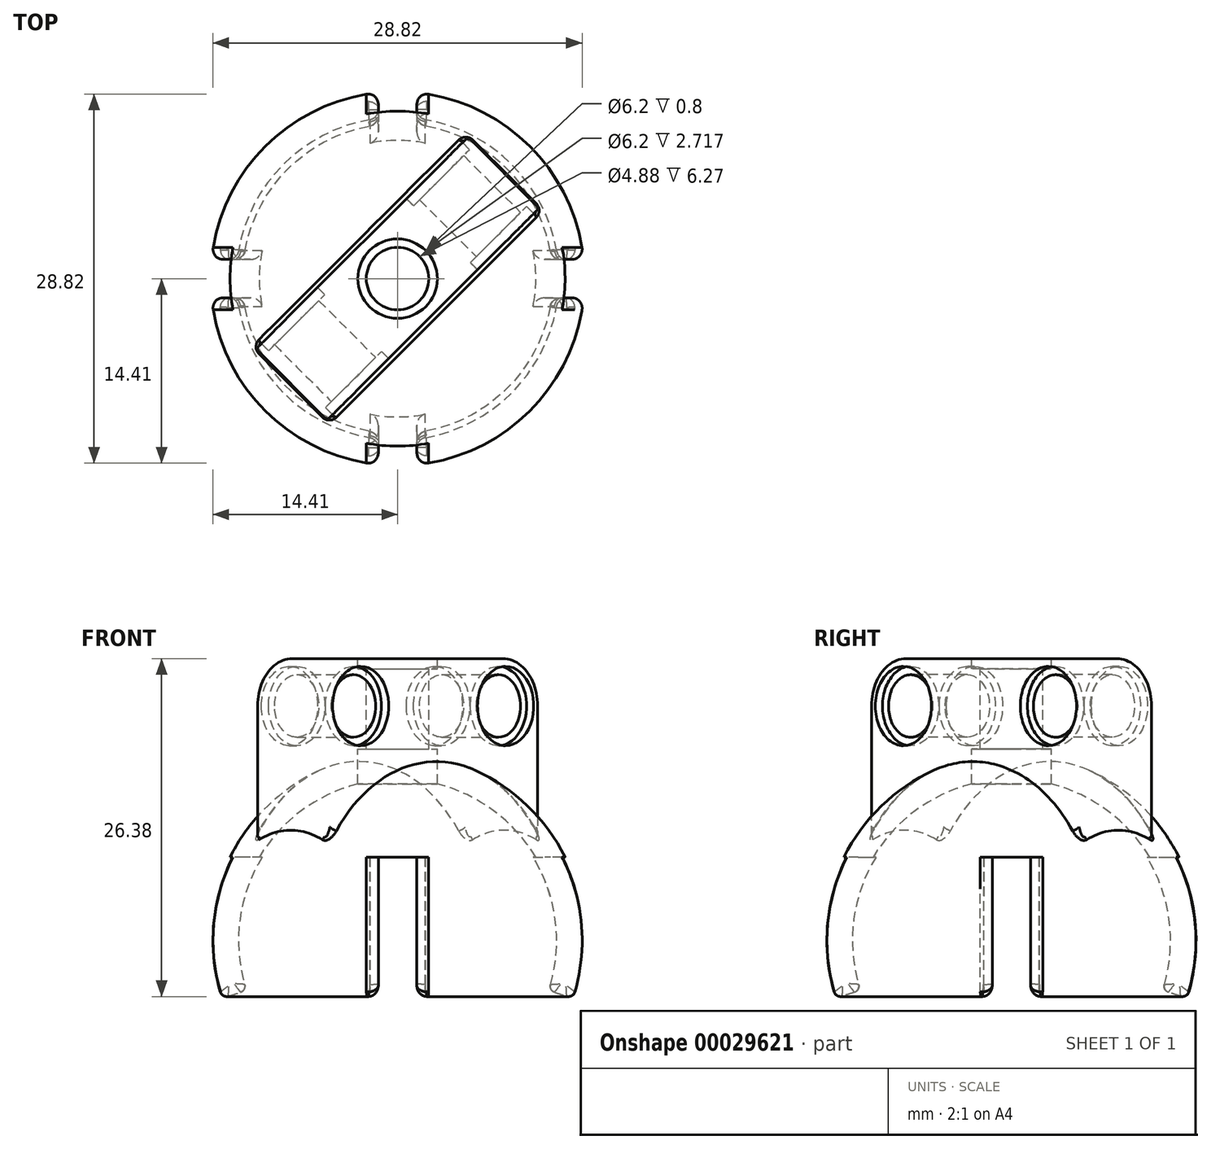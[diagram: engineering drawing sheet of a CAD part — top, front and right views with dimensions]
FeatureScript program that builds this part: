
annotation { "Feature Type Name" : "Feature", "Feature Type Description" : "" }
export const myFeature = defineFeature(function(context is Context, id is Id, definition is map)
    precondition{}
    {
        {
            var Q0;
            Q0=qCreatedBy(makeId("Front.planeOp"),FACE);
            var sketch = newSketch(context, id + "F0", { "sketchPlane" : qUnion([Q0])});
            skArc(sketch, "E0", {"start": v(12.12, -3.43) * mm, "mid": v(10.05, 7.6) * mm, "end": v(0, 12.6) * mm});
            skArc(sketch, "E1", {"start": v(14.04, -4.02) * mm, "mid": v(11.66, 8.79) * mm, "end": v(0, 14.6) * mm});
            skLineSegment(sketch, "E2", {"start": v(12.45, -4.05) * mm, "end": v(13.4, -4.35) * mm});
            skLineSegment(sketch, "E3", {"start": v(0, 0) * mm, "end": v(0, 14.6) * mm, "construction": true});
            skLineSegment(sketch, "E4", {"start": v(0, 14.6) * mm, "end": v(0, 12.6) * mm});
            skArc(sketch, "E5.filletArc", {"start": v(12.12, -3.43) * mm, "mid": v(12.16, -3.8) * mm, "end": v(12.45, -4.05) * mm});
            skPoint(sketch, "E6.visualSharp", {"position": v(13.89, -4.51) * mm});
            skArc(sketch, "E6.filletArc", {"start": v(13.4, -4.35) * mm, "mid": v(13.8, -4.32) * mm, "end": v(14.04, -4.02) * mm});
            skLineSegment(sketch, "E7", {"start": v(12.1, -3.57) * mm, "end": v(12.1, -6.08) * mm, "construction": true});
            skLineSegment(sketch, "E8", {"start": v(12.1, -3.57) * mm, "end": v(11.4, -3.57) * mm, "construction": true});
            skSolve(sketch);
        }
        {
            var Q0;
            Q0=makeQuery(id+"F0.imprint","IMPRINT",FACE,{"disambiguationData":[TD([[makeQuery(id+"F0.imprint","IMPRINT",EDGE,{"derivedFrom":sQuery(id+"F0.wireOp",EDGE,"E0")}),-1.0]])]});
            var Q1;
            Q1=sQuery(id+"F0.wireOp",EDGE,"E3");
            revolve(context, id + "F1", {"entities" : qUnion([Q0]), "axis" : qUnion([Q1]), "revolveType" : RevolveType.FULL});
        }
        {
            var Q0;
            Q0=qCreatedBy(makeId("Top.planeOp"),FACE);
            var sketch = newSketch(context, id + "F2", { "sketchPlane" : qUnion([Q0])});
            skLineSegment(sketch, "E9.rect.bottom", {"start": v(16.14, 1.5) * mm, "end": v(-16.14, 1.5) * mm});
            skLineSegment(sketch, "E9.rect.top", {"start": v(16.14, -1.5) * mm, "end": v(-16.14, -1.5) * mm});
            skLineSegment(sketch, "E9.rect.left", {"start": v(16.14, 1.5) * mm, "end": v(16.14, -1.5) * mm});
            skLineSegment(sketch, "E9.rect.right", {"start": v(-16.14, 1.5) * mm, "end": v(-16.14, -1.5) * mm});
            skPoint(sketch, "E9.rect.middle", {"position": v(0, 0) * mm});
            skLineSegment(sketch, "E10.rect.bottom", {"start": v(1.5, -18.77) * mm, "end": v(-1.5, -18.77) * mm});
            skLineSegment(sketch, "E10.rect.top", {"start": v(1.5, 18.77) * mm, "end": v(-1.5, 18.77) * mm});
            skLineSegment(sketch, "E10.rect.left", {"start": v(1.5, -18.77) * mm, "end": v(1.5, 18.77) * mm});
            skLineSegment(sketch, "E10.rect.right", {"start": v(-1.5, -18.77) * mm, "end": v(-1.5, 18.77) * mm});
            skSolve(sketch);
        }
        {
            var Q0;
            Q0 = qSketchRegion(id + "F2", true);
            extrude(context, id + "F3", {"entities" : qUnion([Q0]), "operationType" : NewBodyOperationType.REMOVE, "endBound" : BoundingType.SYMMETRIC, "oppositeDirection" : true, "depth" : 13 * mm});
        }
        {
            var Q0;
            Q0=qCreatedBy(makeId("Top.planeOp"),FACE);
            var sketch = newSketch(context, id + "F4", { "sketchPlane" : qUnion([Q0])});
            skLineSegment(sketch, "E11", {"start": v(0, 0) * mm, "end": v(-78.4, 78.4) * mm, "construction": true});
            skLineSegment(sketch, "E12", {"start": v(0, 0) * mm, "end": v(-78.9, 0) * mm, "construction": true});
            skSolve(sketch);
        }
        {
            var Q0;
            Q0=sQuery(id+"F4.wireOp",EDGE,"E11");
            var Q1;
            Q1=sQuery(id+"F4.wireOp",VERTEX,"E12.start");
            cPlane(context, id + "F5", {"entities" : qUnion([Q0, Q1]), "cplaneType" : CPlaneType.LINE_POINT, "offset" : 150 * mm, "width" : 150 * mm, "height" : 150 * mm});
        }
        {
            var Q0;
            Q0=qCreatedBy(id+"F5.planeOp",FACE);
            var sketch = newSketch(context, id + "F6", { "sketchPlane" : qUnion([Q0])});
            skArc(sketch, "E13", {"start": v(11.7, 7.69) * mm, "mid": v(0, 14) * mm, "end": v(-11.7, 7.69) * mm});
            skLineSegment(sketch, "E14.rect.bottom", {"start": v(-8, 22) * mm, "end": v(8, 22) * mm});
            skLineSegment(sketch, "E14.rect.left", {"start": v(-11.7, 18.3) * mm, "end": v(-11.7, 7.69) * mm});
            skLineSegment(sketch, "E14.rect.right", {"start": v(11.7, 18.3) * mm, "end": v(11.7, 7.69) * mm});
            skLineSegment(sketch, "E15", {"start": v(0, 0) * mm, "end": v(0, 21.87) * mm, "construction": true});
            skCircle(sketch, "E16", {"center": v(8, 18.3) * mm, "radius": 3.1 * mm});
            skCircle(sketch, "E17.MirrorC", {"center": v(-8, 18.3) * mm, "radius": 3.1 * mm});
            skPoint(sketch, "E18.visualSharp", {"position": v(11.7, 22) * mm});
            skArc(sketch, "E18.filletArc", {"start": v(11.7, 18.3) * mm, "mid": v(10.62, 20.92) * mm, "end": v(8, 22) * mm});
            skPoint(sketch, "E19.visualSharp", {"position": v(-11.7, 22) * mm});
            skArc(sketch, "E19.filletArc", {"start": v(-8, 22) * mm, "mid": v(-10.62, 20.92) * mm, "end": v(-11.7, 18.3) * mm});
            skSolve(sketch);
        }
        {
            var Q0;
            Q0 = qSketchRegion(id + "F6", true);
            extrude(context, id + "F7", {"entities" : qUnion([Q0]), "operationType" : NewBodyOperationType.ADD, "endBound" : BoundingType.SYMMETRIC, "depth" : 7.85 * mm});
        }
        {
            var Q0;
            Q0=qCreatedBy(id+"F5.planeOp",FACE);
            var sketch = newSketch(context, id + "F8", { "sketchPlane" : qUnion([Q0])});
            skCircle(sketch, "E20", {"center": v(8, 18.3) * mm, "radius": 3.41 * mm});
            skCircle(sketch, "E21", {"center": v(8, 18.3) * mm, "radius": 2.44 * mm});
            skCircle(sketch, "E22", {"center": v(-8, 18.3) * mm, "radius": 2.44 * mm});
            skCircle(sketch, "E23", {"center": v(-8, 18.3) * mm, "radius": 3.58 * mm});
            skSolve(sketch);
        }
        {
            var Q0;
            Q0 = qSketchRegion(id + "F8", true);
            extrude(context, id + "F9", {"entities" : qUnion([Q0]), "operationType" : NewBodyOperationType.ADD, "endBound" : BoundingType.SYMMETRIC, "depth" : 6.27 * mm});
        }
        {
            var Q0;
            Q0=makeQuery(id+"F7.opExtrude","SWEPT_FACE",FACE,{"disambiguationData":[OSD([sQuery(id+"F6.wireOp",EDGE,"E14.rect.bottom")])]});
            var sketch = newSketch(context, id + "F10", { "sketchPlane" : qUnion([Q0])});
            skCircle(sketch, "E24", {"center": v(0, 0) * mm, "radius": 3.1 * mm});
            skSolve(sketch);
        }
        {
            var Q0;
            Q0 = qSketchRegion(id + "F10", true);
            extrude(context, id + "F11", {"entities" : qUnion([Q0]), "operationType" : NewBodyOperationType.REMOVE, "endBound" : BoundingType.THROUGH_ALL, "oppositeDirection" : true, "depth" : 25 * mm});
        }
        {
            var Q0;
            Q0=makeQuery(id+"F7.opExtrude","CAP_VERTEX",VERTEX,{"disambiguationData":[OSD([sQuery(id+"F6.wireOp",EDGE,"E14.rect.bottom"),sQuery(id+"F6.wireOp",EDGE,"E18.filletArc")])],"isStart":false});
            var Q1;
            Q1=makeQuery(id+"F7.opExtrude","CAP_VERTEX",VERTEX,{"disambiguationData":[OSD([sQuery(id+"F6.wireOp",EDGE,"E14.rect.bottom"),sQuery(id+"F6.wireOp",EDGE,"E18.filletArc")])],"isStart":true});
            var Q2;
            Q2=makeQuery(id+"F7.opExtrude","CAP_VERTEX",VERTEX,{"disambiguationData":[OSD([sQuery(id+"F6.wireOp",EDGE,"E14.rect.bottom"),sQuery(id+"F6.wireOp",EDGE,"E19.filletArc")])],"isStart":true});
            cPlane(context, id + "F12", {"entities" : qUnion([Q0, Q1, Q2]), "cplaneType" : CPlaneType.THREE_POINT, "offset" : 20 * mm, "width" : 150 * mm, "height" : 150 * mm});
        }
        {
            var Q0;
            Q0=qCreatedBy(id+"F12.planeOp",FACE);
            cPlane(context, id + "F13", {"entities" : qUnion([Q0]), "cplaneType" : CPlaneType.OFFSET, "offset" : 0.8 * mm, "width" : 150 * mm, "height" : 150 * mm});
        }
        {
            var Q0;
            Q0=qCreatedBy(id+"F13.planeOp",FACE);
            var sketch = newSketch(context, id + "F14", { "sketchPlane" : qUnion([Q0])});
            skCircle(sketch, "E25", {"center": v(0, 0) * mm, "radius": 2.44 * mm});
            skCircle(sketch, "E26", {"center": v(0, 0) * mm, "radius": 3.35 * mm});
            skSolve(sketch);
        }
        {
            var Q0;
            Q0 = qSketchRegion(id + "F14", true);
            extrude(context, id + "F15", {"entities" : qUnion([Q0]), "operationType" : NewBodyOperationType.ADD, "depth" : 6.27 * mm});
        }
        {
            var Q0;
            Q0=makeQuery(id+"F7.opExtrude","CAP_EDGE",EDGE,{"disambiguationData":[OSD([sQuery(id+"F6.wireOp",EDGE,"E14.rect.right")])],"isStart":true});
            var Q1;
            Q1=makeQuery(id+"F7.opExtrude","CAP_EDGE",EDGE,{"disambiguationData":[OSD([sQuery(id+"F6.wireOp",EDGE,"E18.filletArc")])],"isStart":true});
            var Q2;
            Q2=makeQuery(id+"F7.opExtrude","CAP_EDGE",EDGE,{"disambiguationData":[OSD([sQuery(id+"F6.wireOp",EDGE,"E14.rect.bottom")])],"isStart":true});
            var Q3;
            Q3=makeQuery(id+"F7.opExtrude","CAP_EDGE",EDGE,{"disambiguationData":[OSD([sQuery(id+"F6.wireOp",EDGE,"E19.filletArc")])],"isStart":true});
            var Q4;
            Q4=makeQuery(id+"F7.opExtrude","CAP_EDGE",EDGE,{"disambiguationData":[OSD([sQuery(id+"F6.wireOp",EDGE,"E14.rect.right")])],"isStart":false});
            fillet(context, id + "F16", {"entities" : qUnion([Q0, Q1, Q2, Q3, Q4]), "radius" : 0.3 * mm, "tangentPropagation" : true, "allowEdgeOverflow" : false});
        }
        {
            var Q0;
            Q0=makeQuery(id+"F7.boolean.opBoolean","INTERSECT",EDGE,{"derivedFrom":[makeQuery(id+"F1.opRevolve","SWEPT_FACE",FACE,{"disambiguationData":[OSD([sQuery(id+"F0.wireOp",EDGE,"E1")])]}),makeQuery(id+"F7.opExtrude","SWEPT_FACE",FACE,{"disambiguationData":[OSD([sQuery(id+"F6.wireOp",EDGE,"E14.rect.left")])]})]});
            fillet(context, id + "F17", {"entities" : qUnion([Q0]), "radius" : .5 * mm, "tangentPropagation" : true, "allowEdgeOverflow" : false});
        }
        {
            var Q0;
            {var subQ0=sQuery(id+"F2.wireOp",EDGE,"E10.rect.left");Q0=makeQuery(id+"F3.boolean.opBoolean","INTERSECT",EDGE,{"derivedFrom":[makeQuery(id+"F1.opRevolve","SWEPT_FACE",FACE,{"disambiguationData":[OSD([sQuery(id+"F0.wireOp",EDGE,"E0")])]}),makeQuery(id+"F3.opExtrude","SWEPT_FACE",FACE,{"disambiguationData":[OSD([subQ0]),TDD([makeQuery(id+"F2.imprint","IMPRINT",EDGE,{"disambiguationData":[TD([[makeQuery(id+"F2.imprint","INTERSECT",VERTEX,{"derivedFrom":[sQuery(id+"F2.wireOp",EDGE,"E10.rect.top"),subQ0]}),1.0]])],"derivedFrom":subQ0})])]})]});}
            var Q1;
            {var subQ0=sQuery(id+"F2.wireOp",EDGE,"E10.rect.right");Q1=makeQuery(id+"F3.boolean.opBoolean","INTERSECT",EDGE,{"derivedFrom":[makeQuery(id+"F1.opRevolve","SWEPT_FACE",FACE,{"disambiguationData":[OSD([sQuery(id+"F0.wireOp",EDGE,"E0")])]}),makeQuery(id+"F3.opExtrude","SWEPT_FACE",FACE,{"disambiguationData":[OSD([subQ0]),TDD([makeQuery(id+"F2.imprint","IMPRINT",EDGE,{"disambiguationData":[TD([[makeQuery(id+"F2.imprint","INTERSECT",VERTEX,{"derivedFrom":[sQuery(id+"F2.wireOp",EDGE,"E10.rect.top"),subQ0]}),1.0]])],"derivedFrom":subQ0})])]})]});}
            var Q2;
            {var subQ0=sQuery(id+"F2.wireOp",EDGE,"E9.rect.bottom");Q2=makeQuery(id+"F3.boolean.opBoolean","INTERSECT",EDGE,{"derivedFrom":[makeQuery(id+"F1.opRevolve","SWEPT_FACE",FACE,{"disambiguationData":[OSD([sQuery(id+"F0.wireOp",EDGE,"E0")])]}),makeQuery(id+"F3.opExtrude","SWEPT_FACE",FACE,{"disambiguationData":[OSD([subQ0]),TDD([makeQuery(id+"F2.imprint","IMPRINT",EDGE,{"disambiguationData":[TD([[makeQuery(id+"F2.imprint","INTERSECT",VERTEX,{"derivedFrom":[subQ0,sQuery(id+"F2.wireOp",EDGE,"E9.rect.right")]}),1.0]])],"derivedFrom":subQ0})])]})]});}
            var Q3;
            {var subQ0=sQuery(id+"F2.wireOp",EDGE,"E9.rect.top");Q3=makeQuery(id+"F3.boolean.opBoolean","INTERSECT",EDGE,{"derivedFrom":[makeQuery(id+"F1.opRevolve","SWEPT_FACE",FACE,{"disambiguationData":[OSD([sQuery(id+"F0.wireOp",EDGE,"E1")])]}),makeQuery(id+"F3.opExtrude","SWEPT_FACE",FACE,{"disambiguationData":[OSD([subQ0]),TDD([makeQuery(id+"F2.imprint","IMPRINT",EDGE,{"disambiguationData":[TD([[makeQuery(id+"F2.imprint","INTERSECT",VERTEX,{"derivedFrom":[subQ0,sQuery(id+"F2.wireOp",EDGE,"E9.rect.right")]}),1.0]])],"derivedFrom":subQ0})])]})]});}
            var Q4;
            {var subQ0=sQuery(id+"F2.wireOp",EDGE,"E10.rect.left");Q4=makeQuery(id+"F3.boolean.opBoolean","INTERSECT",EDGE,{"derivedFrom":[makeQuery(id+"F1.opRevolve","SWEPT_FACE",FACE,{"disambiguationData":[OSD([sQuery(id+"F0.wireOp",EDGE,"E1")])]}),makeQuery(id+"F3.opExtrude","SWEPT_FACE",FACE,{"disambiguationData":[OSD([subQ0]),TDD([makeQuery(id+"F2.imprint","IMPRINT",EDGE,{"disambiguationData":[TD([[makeQuery(id+"F2.imprint","INTERSECT",VERTEX,{"derivedFrom":[sQuery(id+"F2.wireOp",EDGE,"E10.rect.bottom"),subQ0]}),-1.0]])],"derivedFrom":subQ0})])]})]});}
            var Q5;
            {var subQ0=sQuery(id+"F2.wireOp",EDGE,"E10.rect.right");Q5=makeQuery(id+"F3.boolean.opBoolean","INTERSECT",EDGE,{"derivedFrom":[makeQuery(id+"F1.opRevolve","SWEPT_FACE",FACE,{"disambiguationData":[OSD([sQuery(id+"F0.wireOp",EDGE,"E1")])]}),makeQuery(id+"F3.opExtrude","SWEPT_FACE",FACE,{"disambiguationData":[OSD([subQ0]),TDD([makeQuery(id+"F2.imprint","IMPRINT",EDGE,{"disambiguationData":[TD([[makeQuery(id+"F2.imprint","INTERSECT",VERTEX,{"derivedFrom":[sQuery(id+"F2.wireOp",EDGE,"E10.rect.bottom"),subQ0]}),-1.0]])],"derivedFrom":subQ0})])]})]});}
            var Q6;
            {var subQ0=sQuery(id+"F2.wireOp",EDGE,"E9.rect.bottom");Q6=makeQuery(id+"F3.boolean.opBoolean","INTERSECT",EDGE,{"derivedFrom":[makeQuery(id+"F1.opRevolve","SWEPT_FACE",FACE,{"disambiguationData":[OSD([sQuery(id+"F0.wireOp",EDGE,"E1")])]}),makeQuery(id+"F3.opExtrude","SWEPT_FACE",FACE,{"disambiguationData":[OSD([subQ0]),TDD([makeQuery(id+"F2.imprint","IMPRINT",EDGE,{"disambiguationData":[TD([[makeQuery(id+"F2.imprint","INTERSECT",VERTEX,{"derivedFrom":[subQ0,sQuery(id+"F2.wireOp",EDGE,"E9.rect.left")]}),-1.0]])],"derivedFrom":subQ0})])]})]});}
            var Q7;
            {var subQ0=sQuery(id+"F2.wireOp",EDGE,"E9.rect.top");Q7=makeQuery(id+"F3.boolean.opBoolean","INTERSECT",EDGE,{"derivedFrom":[makeQuery(id+"F1.opRevolve","SWEPT_FACE",FACE,{"disambiguationData":[OSD([sQuery(id+"F0.wireOp",EDGE,"E1")])]}),makeQuery(id+"F3.opExtrude","SWEPT_FACE",FACE,{"disambiguationData":[OSD([subQ0]),TDD([makeQuery(id+"F2.imprint","IMPRINT",EDGE,{"disambiguationData":[TD([[makeQuery(id+"F2.imprint","INTERSECT",VERTEX,{"derivedFrom":[subQ0,sQuery(id+"F2.wireOp",EDGE,"E9.rect.left")]}),-1.0]])],"derivedFrom":subQ0})])]})]});}
            fillet(context, id + "F18", {"entities" : qUnion([Q0, Q1, Q2, Q3, Q4, Q5, Q6, Q7]), "radius" : .8 * mm, "tangentPropagation" : true, "allowEdgeOverflow" : false});
        }
    });
